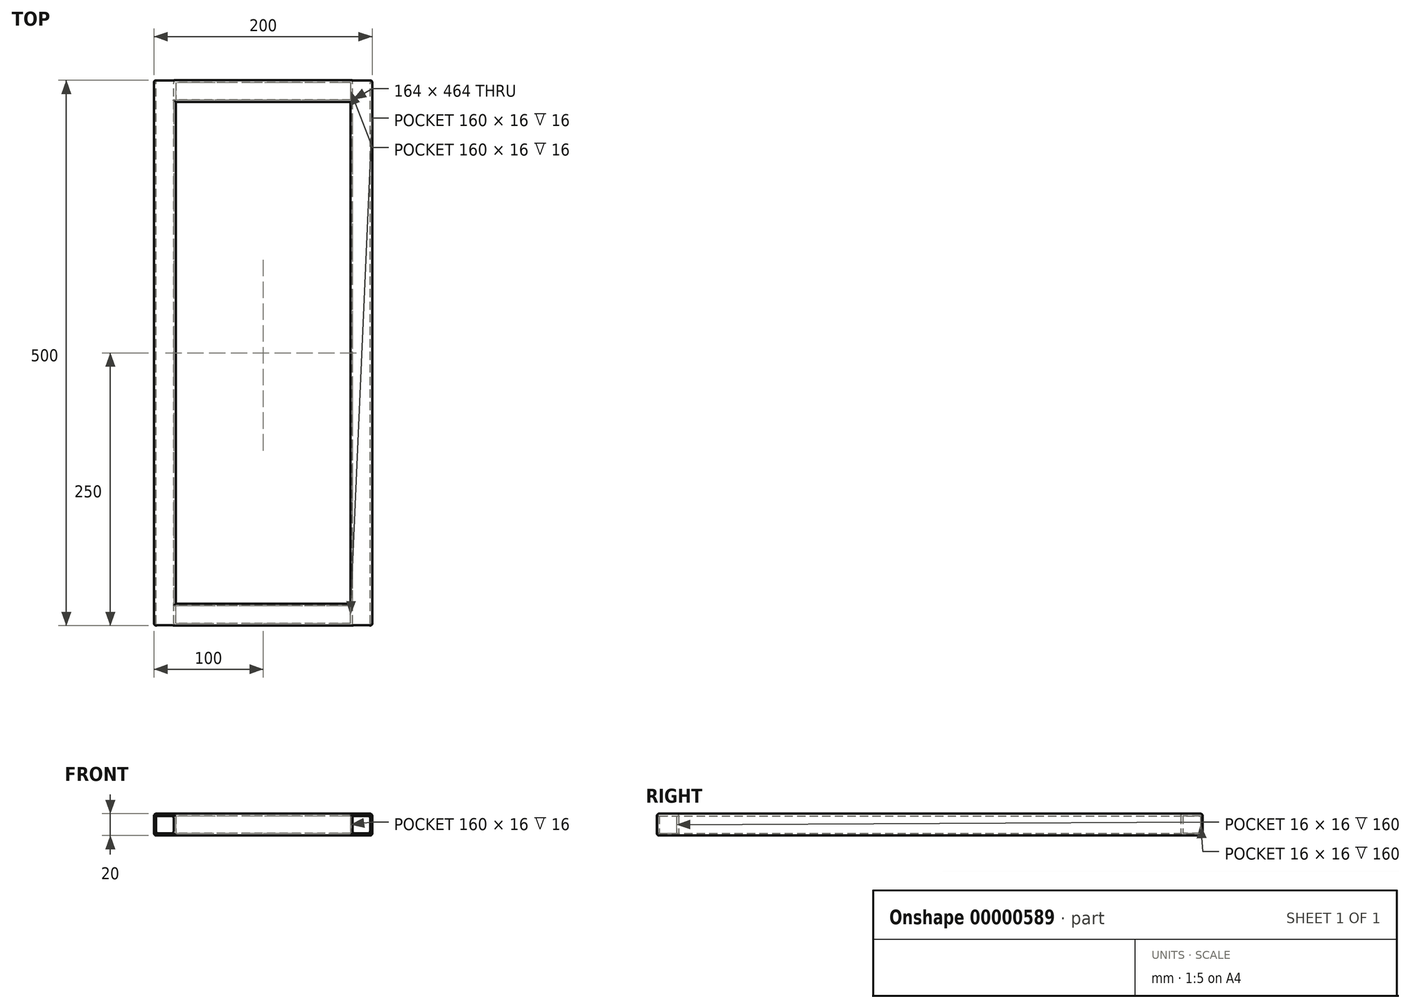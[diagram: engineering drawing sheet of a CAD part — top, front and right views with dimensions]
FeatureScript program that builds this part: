
annotation { "Feature Type Name" : "Feature", "Feature Type Description" : "" }
export const myFeature = defineFeature(function(context is Context, id is Id, definition is map)
    precondition{}
    {
        {
            var Q0;
            Q0 = qCreatedBy(makeId("Front.planeOp"), FACE);
            var sketch = newSketch(context, id + "F0", { "sketchPlane" : qUnion([Q0])});
            skLineSegment(sketch, "E0.rect.bottom", {"start": v(-80, 10) * mm, "end": v(-100, 10) * mm});
            skLineSegment(sketch, "E0.rect.top", {"start": v(-80, -10) * mm, "end": v(-100, -10) * mm});
            skLineSegment(sketch, "E0.rect.left", {"start": v(-80, 10) * mm, "end": v(-80, -10) * mm});
            skLineSegment(sketch, "E0.rect.right", {"start": v(-100, 10) * mm, "end": v(-100, -10) * mm});
            skPoint(sketch, "E0.rect.middle", {"position": v(-90, 0) * mm});
            skLineSegment(sketch, "E1.rect.bottom", {"start": v(-82, 8) * mm, "end": v(-98, 8) * mm});
            skLineSegment(sketch, "E1.rect.top", {"start": v(-82, -8) * mm, "end": v(-98, -8) * mm});
            skLineSegment(sketch, "E1.rect.left", {"start": v(-82, 8) * mm, "end": v(-82, -8) * mm});
            skLineSegment(sketch, "E1.rect.right", {"start": v(-98, 8) * mm, "end": v(-98, -8) * mm});
            skLineSegment(sketch, "E2.rect.bottom", {"start": v(80, 10) * mm, "end": v(100, 10) * mm});
            skLineSegment(sketch, "E2.rect.top", {"start": v(80, -10) * mm, "end": v(100, -10) * mm});
            skLineSegment(sketch, "E2.rect.left", {"start": v(80, 10) * mm, "end": v(80, -10) * mm});
            skLineSegment(sketch, "E2.rect.right", {"start": v(100, 10) * mm, "end": v(100, -10) * mm});
            skPoint(sketch, "E2.rect.middle", {"position": v(90, 0) * mm});
            skLineSegment(sketch, "E3.rect.bottom", {"start": v(82, 8) * mm, "end": v(98, 8) * mm});
            skLineSegment(sketch, "E3.rect.top", {"start": v(82, -8) * mm, "end": v(98, -8) * mm});
            skLineSegment(sketch, "E3.rect.left", {"start": v(82, 8) * mm, "end": v(82, -8) * mm});
            skLineSegment(sketch, "E3.rect.right", {"start": v(98, 8) * mm, "end": v(98, -8) * mm});
            skLineSegment(sketch, "E4", {"start": v(-100, 0) * mm, "end": v(100, 0) * mm, "construction": true});
            skSolve(sketch);
        }
        {
            var Q0;
            Q0=makeQuery(id+"F0.imprint","IMPRINT",FACE,{"disambiguationData":[TD([[makeQuery(id+"F0.imprint","IMPRINT",EDGE,{"derivedFrom":sQuery(id+"F0.wireOp",EDGE,"E0.rect.bottom")}),1.0]])]});
            var Q1;
            Q1=makeQuery(id+"F0.imprint","IMPRINT",FACE,{"disambiguationData":[TD([[makeQuery(id+"F0.imprint","IMPRINT",EDGE,{"derivedFrom":sQuery(id+"F0.wireOp",EDGE,"E2.rect.bottom")}),-1.0]])]});
            extrude(context, id + "F1", {"entities" : qUnion([Q0, Q1]), "endBound" : BoundingType.SYMMETRIC, "depth" : 500 * mm});
        }
        {
            var Q0;
            Q0=makeQuery(id+"F1.opExtrude","SWEPT_FACE",FACE,{"disambiguationData":[OSD([sQuery(id+"F0.wireOp",EDGE,"E0.rect.left")])]});
            var sketch = newSketch(context, id + "F2", { "sketchPlane" : qUnion([Q0])});
            skLineSegment(sketch, "E5.rect.bottom", {"start": v(-250, 10) * mm, "end": v(-230, 10) * mm});
            skLineSegment(sketch, "E5.rect.top", {"start": v(-250, -10) * mm, "end": v(-230, -10) * mm});
            skLineSegment(sketch, "E5.rect.left", {"start": v(-250, 10) * mm, "end": v(-250, -10) * mm});
            skLineSegment(sketch, "E5.rect.right", {"start": v(-230, 10) * mm, "end": v(-230, -10) * mm});
            skPoint(sketch, "E5.rect.middle", {"position": v(-240, 0) * mm});
            skLineSegment(sketch, "E6.rect.bottom", {"start": v(-248, 8) * mm, "end": v(-232, 8) * mm});
            skLineSegment(sketch, "E6.rect.top", {"start": v(-248, -8) * mm, "end": v(-232, -8) * mm});
            skLineSegment(sketch, "E6.rect.left", {"start": v(-248, 8) * mm, "end": v(-248, -8) * mm});
            skLineSegment(sketch, "E6.rect.right", {"start": v(-232, 8) * mm, "end": v(-232, -8) * mm});
            skLineSegment(sketch, "E7.rect.bottom", {"start": v(250, 10) * mm, "end": v(230, 10) * mm});
            skLineSegment(sketch, "E7.rect.top", {"start": v(250, -10) * mm, "end": v(230, -10) * mm});
            skLineSegment(sketch, "E7.rect.left", {"start": v(250, 10) * mm, "end": v(250, -10) * mm});
            skLineSegment(sketch, "E7.rect.right", {"start": v(230, 10) * mm, "end": v(230, -10) * mm});
            skPoint(sketch, "E7.rect.middle", {"position": v(240, 0) * mm});
            skLineSegment(sketch, "E8.rect.bottom", {"start": v(248, 8) * mm, "end": v(232, 8) * mm});
            skLineSegment(sketch, "E8.rect.top", {"start": v(248, -8) * mm, "end": v(232, -8) * mm});
            skLineSegment(sketch, "E8.rect.left", {"start": v(248, 8) * mm, "end": v(248, -8) * mm});
            skLineSegment(sketch, "E8.rect.right", {"start": v(232, 8) * mm, "end": v(232, -8) * mm});
            skSolve(sketch);
        }
        {
            var Q0;
            Q0=makeQuery(id+"F2.imprint","IMPRINT",FACE,{"disambiguationData":[TD([[makeQuery(id+"F2.imprint","IMPRINT",EDGE,{"derivedFrom":sQuery(id+"F2.wireOp",EDGE,"E5.rect.bottom")}),-1.0]])]});
            var Q1;
            Q1=makeQuery(id+"F2.imprint","IMPRINT",FACE,{"disambiguationData":[TD([[makeQuery(id+"F2.imprint","IMPRINT",EDGE,{"derivedFrom":sQuery(id+"F2.wireOp",EDGE,"E7.rect.bottom")}),-1.0]])]});
            extrude(context, id + "F3", {"entities" : qUnion([Q0, Q1]), "operationType" : NewBodyOperationType.ADD, "endBound" : BoundingType.UP_TO_NEXT, "depth" : 25 * mm});
        }
        {
            var Q0;
            Q0=makeQuery(id+"F1.opExtrude","SWEPT_EDGE",EDGE,{"disambiguationData":[OSD([sQuery(id+"F0.wireOp",EDGE,"E0.rect.bottom"),sQuery(id+"F0.wireOp",EDGE,"E0.rect.left")])]});
            var Q1;
            Q1=makeQuery(id+"F1.opExtrude","SWEPT_EDGE",EDGE,{"disambiguationData":[OSD([sQuery(id+"F0.wireOp",EDGE,"E0.rect.top"),sQuery(id+"F0.wireOp",EDGE,"E0.rect.left")])]});
            var Q2;
            Q2=makeQuery(id+"F1.opExtrude","SWEPT_EDGE",EDGE,{"disambiguationData":[OSD([sQuery(id+"F0.wireOp",EDGE,"E0.rect.bottom"),sQuery(id+"F0.wireOp",EDGE,"E0.rect.right")])]});
            var Q3;
            Q3=makeQuery(id+"F1.opExtrude","SWEPT_EDGE",EDGE,{"disambiguationData":[OSD([sQuery(id+"F0.wireOp",EDGE,"E1.rect.top"),sQuery(id+"F0.wireOp",EDGE,"E1.rect.right")])]});
            var Q4;
            Q4=makeQuery(id+"F1.opExtrude","SWEPT_EDGE",EDGE,{"disambiguationData":[OSD([sQuery(id+"F0.wireOp",EDGE,"E1.rect.bottom"),sQuery(id+"F0.wireOp",EDGE,"E1.rect.right")])]});
            var Q5;
            Q5=makeQuery(id+"F1.opExtrude","SWEPT_EDGE",EDGE,{"disambiguationData":[OSD([sQuery(id+"F0.wireOp",EDGE,"E1.rect.bottom"),sQuery(id+"F0.wireOp",EDGE,"E1.rect.left")])]});
            var Q6;
            Q6=makeQuery(id+"F1.opExtrude","SWEPT_EDGE",EDGE,{"disambiguationData":[OSD([sQuery(id+"F0.wireOp",EDGE,"E0.rect.top"),sQuery(id+"F0.wireOp",EDGE,"E0.rect.right")])]});
            var Q7;
            Q7=makeQuery(id+"F1.opExtrude","SWEPT_EDGE",EDGE,{"disambiguationData":[OSD([sQuery(id+"F0.wireOp",EDGE,"E1.rect.top"),sQuery(id+"F0.wireOp",EDGE,"E1.rect.left")])]});
            var Q8;
            Q8=makeQuery(id+"F1.opExtrude","SWEPT_EDGE",EDGE,{"disambiguationData":[OSD([sQuery(id+"F0.wireOp",EDGE,"E2.rect.top"),sQuery(id+"F0.wireOp",EDGE,"E2.rect.left")])]});
            var Q9;
            Q9=makeQuery(id+"F1.opExtrude","SWEPT_EDGE",EDGE,{"disambiguationData":[OSD([sQuery(id+"F0.wireOp",EDGE,"E2.rect.bottom"),sQuery(id+"F0.wireOp",EDGE,"E2.rect.left")])]});
            var Q10;
            Q10=makeQuery(id+"F1.opExtrude","SWEPT_EDGE",EDGE,{"disambiguationData":[OSD([sQuery(id+"F0.wireOp",EDGE,"E2.rect.bottom"),sQuery(id+"F0.wireOp",EDGE,"E2.rect.right")])]});
            var Q11;
            Q11=makeQuery(id+"F1.opExtrude","SWEPT_EDGE",EDGE,{"disambiguationData":[OSD([sQuery(id+"F0.wireOp",EDGE,"E3.rect.top"),sQuery(id+"F0.wireOp",EDGE,"E3.rect.right")])]});
            var Q12;
            Q12=makeQuery(id+"F1.opExtrude","SWEPT_EDGE",EDGE,{"disambiguationData":[OSD([sQuery(id+"F0.wireOp",EDGE,"E3.rect.bottom"),sQuery(id+"F0.wireOp",EDGE,"E3.rect.right")])]});
            var Q13;
            Q13=makeQuery(id+"F1.opExtrude","SWEPT_EDGE",EDGE,{"disambiguationData":[OSD([sQuery(id+"F0.wireOp",EDGE,"E3.rect.bottom"),sQuery(id+"F0.wireOp",EDGE,"E3.rect.left")])]});
            var Q14;
            Q14=makeQuery(id+"F1.opExtrude","SWEPT_EDGE",EDGE,{"disambiguationData":[OSD([sQuery(id+"F0.wireOp",EDGE,"E2.rect.top"),sQuery(id+"F0.wireOp",EDGE,"E2.rect.right")])]});
            var Q15;
            Q15=makeQuery(id+"F1.opExtrude","SWEPT_EDGE",EDGE,{"disambiguationData":[OSD([sQuery(id+"F0.wireOp",EDGE,"E3.rect.top"),sQuery(id+"F0.wireOp",EDGE,"E3.rect.left")])]});
            var Q16;
            Q16=makeQuery(id+"F3.opExtrude","SWEPT_EDGE",EDGE,{"disambiguationData":[OSD([sQuery(id+"F0.wireOp",EDGE,"E0.rect.top"),sQuery(id+"F0.wireOp",EDGE,"E0.rect.left"),sQuery(id+"F2.wireOp",EDGE,"E7.rect.top"),sQuery(id+"F2.wireOp",EDGE,"E7.rect.right")])]});
            var Q17;
            Q17=makeQuery(id+"F3.opExtrude","SWEPT_EDGE",EDGE,{"disambiguationData":[OSD([sQuery(id+"F0.wireOp",EDGE,"E0.rect.bottom"),sQuery(id+"F0.wireOp",EDGE,"E0.rect.left"),sQuery(id+"F2.wireOp",EDGE,"E7.rect.bottom"),sQuery(id+"F2.wireOp",EDGE,"E7.rect.right")])]});
            var Q18;
            {var subQ0=sQuery(id+"F0.wireOp",EDGE,"E2.rect.bottom");Q18=makeQuery(id+"F3.boolean.opBoolean","MERGE",EDGE,{"derivedFrom":[makeQuery(id+"F1.opExtrude","CAP_EDGE",EDGE,{"disambiguationData":[OSD([sQuery(id+"F0.wireOp",EDGE,"E0.rect.bottom")])],"isStart":true}),makeQuery(id+"F1.opExtrude","CAP_EDGE",EDGE,{"disambiguationData":[OSD([subQ0])],"isStart":true}),makeQuery(id+"F3.opExtrude","SWEPT_EDGE",EDGE,{"disambiguationData":[OSD([subQ0,sQuery(id+"F0.wireOp",EDGE,"E2.rect.left")])]})]});}
            var Q19;
            {var subQ0=sQuery(id+"F0.wireOp",EDGE,"E2.rect.top");Q19=makeQuery(id+"F3.boolean.opBoolean","MERGE",EDGE,{"derivedFrom":[makeQuery(id+"F1.opExtrude","CAP_EDGE",EDGE,{"disambiguationData":[OSD([sQuery(id+"F0.wireOp",EDGE,"E0.rect.top")])],"isStart":true}),makeQuery(id+"F1.opExtrude","CAP_EDGE",EDGE,{"disambiguationData":[OSD([subQ0])],"isStart":true}),makeQuery(id+"F3.opExtrude","SWEPT_EDGE",EDGE,{"disambiguationData":[OSD([subQ0,sQuery(id+"F0.wireOp",EDGE,"E2.rect.left")])]})]});}
            var Q20;
            Q20=makeQuery(id+"F3.opExtrude","SWEPT_EDGE",EDGE,{"disambiguationData":[OSD([sQuery(id+"F0.wireOp",EDGE,"E0.rect.top"),sQuery(id+"F0.wireOp",EDGE,"E0.rect.left"),sQuery(id+"F2.wireOp",EDGE,"E5.rect.top"),sQuery(id+"F2.wireOp",EDGE,"E5.rect.right")])]});
            var Q21;
            Q21=makeQuery(id+"F3.opExtrude","SWEPT_EDGE",EDGE,{"disambiguationData":[OSD([sQuery(id+"F0.wireOp",EDGE,"E0.rect.bottom"),sQuery(id+"F0.wireOp",EDGE,"E0.rect.left"),sQuery(id+"F2.wireOp",EDGE,"E5.rect.bottom"),sQuery(id+"F2.wireOp",EDGE,"E5.rect.right")])]});
            var Q22;
            Q22=makeQuery(id+"F3.boolean.opBoolean","MERGE",EDGE,{"derivedFrom":[makeQuery(id+"F1.opExtrude","CAP_EDGE",EDGE,{"disambiguationData":[OSD([sQuery(id+"F0.wireOp",EDGE,"E0.rect.top")])],"isStart":false}),makeQuery(id+"F1.opExtrude","CAP_EDGE",EDGE,{"disambiguationData":[OSD([sQuery(id+"F0.wireOp",EDGE,"E2.rect.top")])],"isStart":false}),makeQuery(id+"F3.opExtrude","SWEPT_EDGE",EDGE,{"disambiguationData":[OSD([sQuery(id+"F2.wireOp",EDGE,"E5.rect.top"),sQuery(id+"F2.wireOp",EDGE,"E5.rect.left")])]})]});
            var Q23;
            Q23=makeQuery(id+"F3.boolean.opBoolean","MERGE",EDGE,{"derivedFrom":[makeQuery(id+"F1.opExtrude","CAP_EDGE",EDGE,{"disambiguationData":[OSD([sQuery(id+"F0.wireOp",EDGE,"E0.rect.bottom")])],"isStart":false}),makeQuery(id+"F1.opExtrude","CAP_EDGE",EDGE,{"disambiguationData":[OSD([sQuery(id+"F0.wireOp",EDGE,"E2.rect.bottom")])],"isStart":false}),makeQuery(id+"F3.opExtrude","SWEPT_EDGE",EDGE,{"disambiguationData":[OSD([sQuery(id+"F2.wireOp",EDGE,"E5.rect.bottom"),sQuery(id+"F2.wireOp",EDGE,"E5.rect.left")])]})]});
            var Q24;
            Q24=makeQuery(id+"F1.opExtrude","CAP_EDGE",EDGE,{"disambiguationData":[OSD([sQuery(id+"F0.wireOp",EDGE,"E0.rect.right")])],"isStart":false});
            var Q25;
            Q25=makeQuery(id+"F1.opExtrude","CAP_EDGE",EDGE,{"disambiguationData":[OSD([sQuery(id+"F0.wireOp",EDGE,"E1.rect.right")])],"isStart":false});
            var Q26;
            Q26=makeQuery(id+"F1.opExtrude","CAP_EDGE",EDGE,{"disambiguationData":[OSD([sQuery(id+"F0.wireOp",EDGE,"E1.rect.bottom")])],"isStart":false});
            var Q27;
            Q27=makeQuery(id+"F1.opExtrude","CAP_EDGE",EDGE,{"disambiguationData":[OSD([sQuery(id+"F0.wireOp",EDGE,"E1.rect.left")])],"isStart":false});
            var Q28;
            Q28=makeQuery(id+"F1.opExtrude","CAP_EDGE",EDGE,{"disambiguationData":[OSD([sQuery(id+"F0.wireOp",EDGE,"E1.rect.top")])],"isStart":false});
            var Q29;
            Q29=makeQuery(id+"F1.opExtrude","CAP_EDGE",EDGE,{"disambiguationData":[OSD([sQuery(id+"F0.wireOp",EDGE,"E3.rect.bottom")])],"isStart":false});
            var Q30;
            Q30=makeQuery(id+"F1.opExtrude","CAP_EDGE",EDGE,{"disambiguationData":[OSD([sQuery(id+"F0.wireOp",EDGE,"E3.rect.left")])],"isStart":false});
            var Q31;
            Q31=makeQuery(id+"F1.opExtrude","CAP_EDGE",EDGE,{"disambiguationData":[OSD([sQuery(id+"F0.wireOp",EDGE,"E3.rect.top")])],"isStart":false});
            var Q32;
            Q32=makeQuery(id+"F1.opExtrude","CAP_EDGE",EDGE,{"disambiguationData":[OSD([sQuery(id+"F0.wireOp",EDGE,"E3.rect.right")])],"isStart":false});
            var Q33;
            Q33=makeQuery(id+"F1.opExtrude","CAP_EDGE",EDGE,{"disambiguationData":[OSD([sQuery(id+"F0.wireOp",EDGE,"E2.rect.right")])],"isStart":false});
            var Q34;
            Q34=makeQuery(id+"F1.opExtrude","CAP_EDGE",EDGE,{"disambiguationData":[OSD([sQuery(id+"F0.wireOp",EDGE,"E3.rect.left")])],"isStart":true});
            var Q35;
            Q35=makeQuery(id+"F1.opExtrude","CAP_EDGE",EDGE,{"disambiguationData":[OSD([sQuery(id+"F0.wireOp",EDGE,"E3.rect.bottom")])],"isStart":true});
            var Q36;
            Q36=makeQuery(id+"F1.opExtrude","CAP_EDGE",EDGE,{"disambiguationData":[OSD([sQuery(id+"F0.wireOp",EDGE,"E3.rect.right")])],"isStart":true});
            var Q37;
            Q37=makeQuery(id+"F1.opExtrude","CAP_EDGE",EDGE,{"disambiguationData":[OSD([sQuery(id+"F0.wireOp",EDGE,"E2.rect.right")])],"isStart":true});
            var Q38;
            Q38=makeQuery(id+"F1.opExtrude","CAP_EDGE",EDGE,{"disambiguationData":[OSD([sQuery(id+"F0.wireOp",EDGE,"E3.rect.top")])],"isStart":true});
            var Q39;
            Q39=makeQuery(id+"F1.opExtrude","CAP_EDGE",EDGE,{"disambiguationData":[OSD([sQuery(id+"F0.wireOp",EDGE,"E0.rect.right")])],"isStart":true});
            var Q40;
            Q40=makeQuery(id+"F1.opExtrude","CAP_EDGE",EDGE,{"disambiguationData":[OSD([sQuery(id+"F0.wireOp",EDGE,"E1.rect.right")])],"isStart":true});
            var Q41;
            Q41=makeQuery(id+"F1.opExtrude","CAP_EDGE",EDGE,{"disambiguationData":[OSD([sQuery(id+"F0.wireOp",EDGE,"E1.rect.bottom")])],"isStart":true});
            var Q42;
            Q42=makeQuery(id+"F1.opExtrude","CAP_EDGE",EDGE,{"disambiguationData":[OSD([sQuery(id+"F0.wireOp",EDGE,"E1.rect.left")])],"isStart":true});
            var Q43;
            Q43=makeQuery(id+"F1.opExtrude","CAP_EDGE",EDGE,{"disambiguationData":[OSD([sQuery(id+"F0.wireOp",EDGE,"E1.rect.top")])],"isStart":true});
            fillet(context, id + "F4", {"entities" : qUnion([Q0, Q1, Q2, Q3, Q4, Q5, Q6, Q7, Q8, Q9, Q10, Q11, Q12, Q13, Q14, Q15, Q16, Q17, Q18, Q19, Q20, Q21, Q22, Q23, Q24, Q25, Q26, Q27, Q28, Q29, Q30, Q31, Q32, Q33, Q34, Q35, Q36, Q37, Q38, Q39, Q40, Q41, Q42, Q43]), "radius" : 2 * mm, "tangentPropagation" : true, "allowEdgeOverflow" : false});
        }
    });
